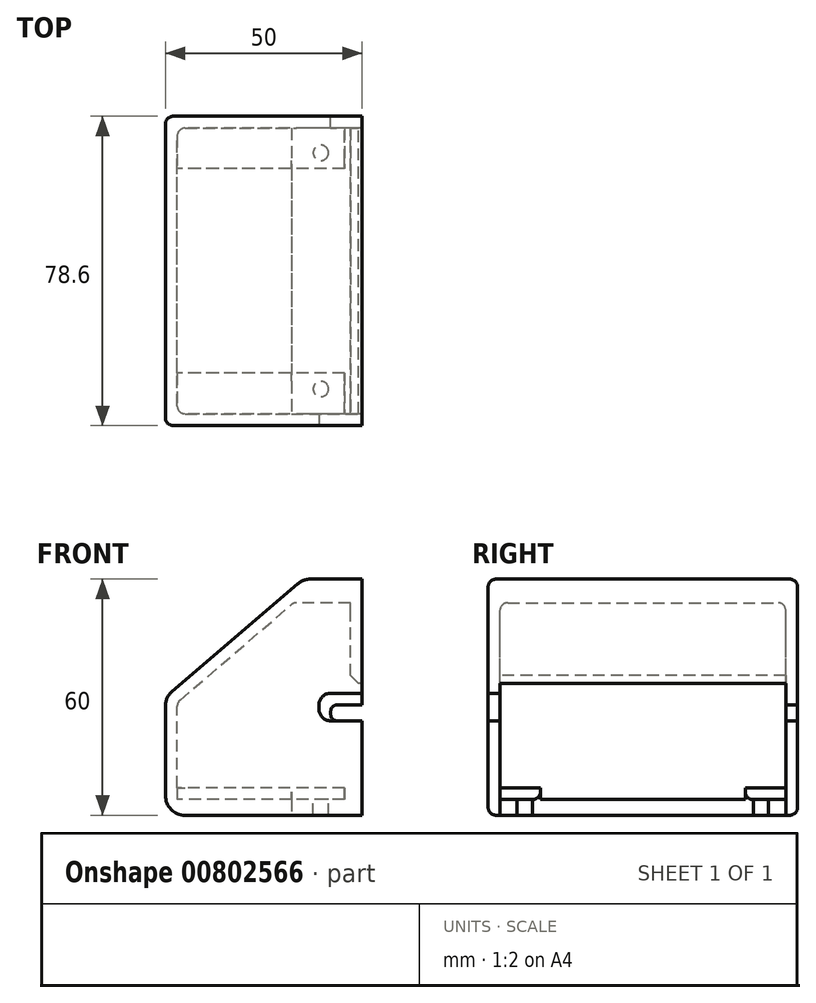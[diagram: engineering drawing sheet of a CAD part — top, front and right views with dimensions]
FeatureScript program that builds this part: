
annotation { "Feature Type Name" : "Feature", "Feature Type Description" : "" }
export const myFeature = defineFeature(function(context is Context, id is Id, definition is map)
    precondition{}
    {
        {
            var Q0;
            Q0=qCreatedBy(makeId("Front.planeOp"),FACE);
            var sketch = newSketch(context, id + "F0", { "sketchPlane" : qUnion([Q0])});
            skLineSegment(sketch, "E0", {"start": v(0, 0) * mm, "end": v(-50, 0) * mm});
            skLineSegment(sketch, "E1", {"start": v(-50, 0) * mm, "end": v(-50, 30) * mm});
            skLineSegment(sketch, "E2", {"start": v(0, 0) * mm, "end": v(0, 60) * mm});
            skLineSegment(sketch, "E3", {"start": v(0, 60) * mm, "end": v(-15, 60) * mm});
            skLineSegment(sketch, "E4", {"start": v(-50, 30) * mm, "end": v(-15, 60) * mm});
            skSolve(sketch);
        }
        {
            var Q0;
            Q0=qSketchRegion(id+"F0",true);
            extrude(context, id + "F1", {"entities" : qUnion([Q0]), "depth" : 78.6 * mm, "offsetDistance" : 25 * mm});
        }
        {
            var Q0;
            Q0=qCreatedBy(makeId("Front.planeOp"),FACE);
            cPlane(context, id + "F2", {"entities" : qUnion([Q0]), "cplaneType" : CPlaneType.OFFSET, "offset" : 3 * mm, "width" : 150 * mm, "height" : 150 * mm});
        }
        {
            var Q0;
            Q0=qCreatedBy(id+"F2.planeOp",FACE);
            var sketch = newSketch(context, id + "F3", { "sketchPlane" : qUnion([Q0])});
            skLineSegment(sketch, "E5", {"start": v(0, 0) * mm, "end": v(0, 4) * mm, "construction": true});
            skLineSegment(sketch, "E6", {"start": v(0, 4) * mm, "end": v(-47, 4) * mm});
            skLineSegment(sketch, "E7", {"start": v(0, 4) * mm, "end": v(0, 33.5) * mm});
            skLineSegment(sketch, "E8", {"start": v(0, 33.5) * mm, "end": v(-3, 33.5) * mm});
            skLineSegment(sketch, "E9", {"start": v(-3, 33.5) * mm, "end": v(-3, 54) * mm});
            skLineSegment(sketch, "E10.0", {"start": v(-47, 28.62) * mm, "end": v(-17.4, 54) * mm});
            skLineSegment(sketch, "E11", {"start": v(-3, 54) * mm, "end": v(-17.4, 54) * mm});
            skLineSegment(sketch, "E12", {"start": v(-47, 4) * mm, "end": v(-47, 28.62) * mm});
            skPoint(sketch, "E13", {"position": v(-47, 28.62) * mm});
            skPoint(sketch, "E14", {"position": v(-17.4, 54) * mm});
            skSolve(sketch);
        }
        {
            var Q0;
            Q0=qSketchRegion(id+"F3",true);
            extrude(context, id + "F4", {"entities" : qUnion([Q0]), "operationType" : NewBodyOperationType.REMOVE, "depth" : 72.6 * mm, "offsetDistance" : 25 * mm});
        }
        {
            var Q0;
            Q0=makeQuery(id+"F1.opExtrude","SWEPT_FACE",FACE,{"disambiguationData":[OSD([sQuery(id+"F0.wireOp",EDGE,"E0")])]});
            var sketch = newSketch(context, id + "F5", { "sketchPlane" : qUnion([Q0])});
            skLineSegment(sketch, "E15", {"start": v(0, 0) * mm, "end": v(0, 3) * mm, "construction": true});
            skLineSegment(sketch, "E16", {"start": v(0, 3) * mm, "end": v(-18, 3) * mm});
            skLineSegment(sketch, "E17", {"start": v(-18, 3) * mm, "end": v(-18, 75.6) * mm});
            skLineSegment(sketch, "E18", {"start": v(-18, 75.6) * mm, "end": v(0, 75.6) * mm});
            skLineSegment(sketch, "E19", {"start": v(0, 75.6) * mm, "end": v(0, 3) * mm});
            skSolve(sketch);
        }
        {
            var Q0;
            Q0=qSketchRegion(id+"F5",true);
            extrude(context, id + "F6", {"entities" : qUnion([Q0]), "operationType" : NewBodyOperationType.REMOVE, "oppositeDirection" : true, "depth" : 5 * mm, "offsetDistance" : 25 * mm});
        }
        {
            var Q0;
            Q0=qCreatedBy(makeId("Front.planeOp"),FACE);
            var sketch = newSketch(context, id + "F7", { "sketchPlane" : qUnion([Q0])});
            skLineSegment(sketch, "E20", {"start": v(0, 0) * mm, "end": v(0, 24) * mm, "construction": true});
            skLineSegment(sketch, "E21", {"start": v(0, 24) * mm, "end": v(0, 28) * mm});
            skLineSegment(sketch, "E22", {"start": v(0, 28) * mm, "end": v(-6.5, 28) * mm});
            skLineSegment(sketch, "E23", {"start": v(-8, 26.5) * mm, "end": v(-8, 25.5) * mm});
            skLineSegment(sketch, "E24", {"start": v(-6.5, 24) * mm, "end": v(0, 24) * mm});
            skPoint(sketch, "E25.visualSharp", {"position": v(-8, 28) * mm});
            skArc(sketch, "E25.filletArc", {"start": v(-6.5, 28) * mm, "mid": v(-7.56, 27.56) * mm, "end": v(-8, 26.5) * mm});
            skPoint(sketch, "E26.visualSharp", {"position": v(-8, 24) * mm});
            skArc(sketch, "E26.filletArc", {"start": v(-8, 25.5) * mm, "mid": v(-7.56, 24.44) * mm, "end": v(-6.5, 24) * mm});
            skSolve(sketch);
        }
        {
            var Q0;
            Q0=qSketchRegion(id+"F7",true);
            extrude(context, id + "F8", {"entities" : qUnion([Q0]), "operationType" : NewBodyOperationType.REMOVE, "depth" : 5 * mm, "offsetDistance" : 25 * mm});
        }
        {
            var Q0;
            Q0=makeQuery(id+"F1.opExtrude","CAP_FACE",FACE,{"disambiguationData":[OSD([sQuery(id+"F0.wireOp",EDGE,"E0"),sQuery(id+"F0.wireOp",EDGE,"E1"),sQuery(id+"F0.wireOp",EDGE,"E2"),sQuery(id+"F0.wireOp",EDGE,"E3"),sQuery(id+"F0.wireOp",EDGE,"E4")])],"isStart":false});
            var sketch = newSketch(context, id + "F9", { "sketchPlane" : qUnion([Q0])});
            skLineSegment(sketch, "E27", {"start": v(0, 0) * mm, "end": v(0, 24) * mm, "construction": true});
            skLineSegment(sketch, "E28", {"start": v(0, 24) * mm, "end": v(0, 31) * mm});
            skLineSegment(sketch, "E29", {"start": v(0, 31) * mm, "end": v(-8, 31) * mm});
            skLineSegment(sketch, "E30", {"start": v(-11, 28) * mm, "end": v(-11, 27) * mm});
            skLineSegment(sketch, "E31", {"start": v(-8, 24) * mm, "end": v(0, 24) * mm});
            skPoint(sketch, "E32.visualSharp", {"position": v(-11, 31) * mm});
            skArc(sketch, "E32.filletArc", {"start": v(-8, 31) * mm, "mid": v(-10.12, 30.12) * mm, "end": v(-11, 28) * mm});
            skPoint(sketch, "E33.visualSharp", {"position": v(-11, 24) * mm});
            skArc(sketch, "E33.filletArc", {"start": v(-11, 27) * mm, "mid": v(-10.12, 24.88) * mm, "end": v(-8, 24) * mm});
            skSolve(sketch);
        }
        {
            var Q0;
            Q0=qSketchRegion(id+"F9",true);
            extrude(context, id + "F10", {"entities" : qUnion([Q0]), "operationType" : NewBodyOperationType.REMOVE, "oppositeDirection" : true, "depth" : 5 * mm, "offsetDistance" : 25 * mm});
        }
        {
            var Q0;
            Q0=makeQuery(id+"FDUO0lFtGd0GRl6_1.opExtrude","CAP_EDGE",EDGE,{"disambiguationData":[OSD([sQuery(id+"Fsfc9BGz6BYfI3k_1.wireOp",EDGE,"UFiVrUBC-8SW0-h0nN-MmJQ-qNYJqojKAnSs")])],"isStart":false});
            var Q1;
            Q1=makeQuery(id+"FDUO0lFtGd0GRl6_1.opExtrude","CAP_EDGE",EDGE,{"disambiguationData":[OSD([sQuery(id+"Fsfc9BGz6BYfI3k_1.wireOp",EDGE,"PaZ7k8qZ-ZSND-94ED-79B7-tNz9TaCtnb4N")])],"isStart":false});
            var Q2;
            Q2=makeQuery(id+"F1.opExtrude","SWEPT_EDGE",EDGE,{"disambiguationData":[OSD([sQuery(id+"F0.wireOp",EDGE,"E3"),sQuery(id+"F0.wireOp",EDGE,"E4")])]});
            var Q3;
            Q3=makeQuery(id+"F1.opExtrude","SWEPT_EDGE",EDGE,{"disambiguationData":[OSD([sQuery(id+"F0.wireOp",EDGE,"E1"),sQuery(id+"F0.wireOp",EDGE,"E4")])]});
            var Q4;
            Q4=makeQuery(id+"F1.opExtrude","SWEPT_EDGE",EDGE,{"disambiguationData":[OSD([sQuery(id+"F0.wireOp",EDGE,"E0"),sQuery(id+"F0.wireOp",EDGE,"E1")])]});
            fillet(context, id + "F11", {"entities" : qUnion([Q0, Q1, Q2, Q3, Q4]), "radius" : 5 * mm, "tangentPropagation" : true, "allowEdgeOverflow" : false});
        }
        {
            var Q0;
            Q0=makeQuery(id+"FDUO0lFtGd0GRl6_1.opExtrude","SWEPT_EDGE",EDGE,{"disambiguationData":[OSD([sQuery(id+"Fsfc9BGz6BYfI3k_1.wireOp",EDGE,"2MNWM4fN-UouW-SbYd-ouZd-wXEaQsLsKWml"),sQuery(id+"Fsfc9BGz6BYfI3k_1.wireOp",EDGE,"UFiVrUBC-8SW0-h0nN-MmJQ-qNYJqojKAnSs")])]});
            var Q1;
            Q1=makeQuery(id+"F1.opExtrude","CAP_EDGE",EDGE,{"disambiguationData":[OSD([sQuery(id+"F0.wireOp",EDGE,"E4")])],"isStart":true});
            var Q2;
            Q2=makeQuery(id+"F1.opExtrude","CAP_EDGE",EDGE,{"disambiguationData":[OSD([sQuery(id+"F0.wireOp",EDGE,"E4")])],"isStart":false});
            fillet(context, id + "F12", {"entities" : qUnion([Q0, Q1, Q2]), "radius" : 2 * mm, "tangentPropagation" : true, "allowEdgeOverflow" : false});
        }
        {
            var Q0;
            Q0=makeQuery(id+"F4.boolean.opBoolean","COPY",FACE,{"derivedFrom":makeQuery(id+"F4.opExtrude","SWEPT_FACE",FACE,{"disambiguationData":[OSD([sQuery(id+"F3.wireOp",EDGE,"E12")])]})});
            var sketch = newSketch(context, id + "F13", { "sketchPlane" : qUnion([Q0])});
            skLineSegment(sketch, "E34", {"start": v(0, 0) * mm, "end": v(-3, 0) * mm, "construction": true});
            skLineSegment(sketch, "E35", {"start": v(-75.6, 0) * mm, "end": v(-78.6, 0) * mm, "construction": true});
            skLineSegment(sketch, "E36", {"start": v(-3, 0) * mm, "end": v(-39.3, 0) * mm, "construction": true});
            skLineSegment(sketch, "E37", {"start": v(-39.3, 0) * mm, "end": v(-39.3, 4) * mm, "construction": true});
            skLineSegment(sketch, "E38", {"start": v(-39.3, 4) * mm, "end": v(-39.3, 7) * mm, "construction": true});
            skLineSegment(sketch, "E39", {"start": v(-39.3, 7) * mm, "end": v(-3, 7) * mm, "construction": true});
            skLineSegment(sketch, "E40", {"start": v(-3, 7) * mm, "end": v(-13.3, 7) * mm});
            skLineSegment(sketch, "E41", {"start": v(-13.3, 7) * mm, "end": v(-13.3, 4) * mm});
            skLineSegment(sketch, "E42", {"start": v(-13.3, 4) * mm, "end": v(-3, 4) * mm});
            skLineSegment(sketch, "E43", {"start": v(-3, 4) * mm, "end": v(-3, 7) * mm});
            skLineSegment(sketch, "E44.MirrorCS", {"start": v(-75.6, 4) * mm, "end": v(-75.6, 7) * mm});
            skLineSegment(sketch, "E45.MirrorCS", {"start": v(-65.3, 7) * mm, "end": v(-65.3, 4) * mm});
            skLineSegment(sketch, "E46.MirrorCS", {"start": v(-65.3, 4) * mm, "end": v(-75.6, 4) * mm});
            skLineSegment(sketch, "E47", {"start": v(-65.3, 7) * mm, "end": v(-75.6, 7) * mm});
            skSolve(sketch);
        }
        {
            var Q0;
            Q0=qSketchRegion(id+"F13",true);
            extrude(context, id + "F14", {"entities" : qUnion([Q0]), "operationType" : NewBodyOperationType.ADD, "depth" : 42.5 * mm, "offsetDistance" : 25 * mm});
        }
        {
            var Q0;
            Q0=qCreatedBy(makeId("Top.planeOp"),FACE);
            cPlane(context, id + "F15", {"entities" : qUnion([Q0]), "cplaneType" : CPlaneType.OFFSET, "offset" : 4 * mm, "width" : 150 * mm, "height" : 150 * mm});
        }
        {
            var Q0;
            Q0=qCreatedBy(id+"F15.planeOp",FACE);
            var sketch = newSketch(context, id + "F16", { "sketchPlane" : qUnion([Q0])});
            skLineSegment(sketch, "E48", {"start": v(0, 0) * mm, "end": v(0, -3) * mm, "construction": true});
            skLineSegment(sketch, "E49", {"start": v(0, -3) * mm, "end": v(-4, -3) * mm, "construction": true});
            skLineSegment(sketch, "E50", {"start": v(-4, -3) * mm, "end": v(-10.5, -3) * mm, "construction": true});
            skLineSegment(sketch, "E51", {"start": v(-10.5, -3) * mm, "end": v(-10.5, -3.3) * mm, "construction": true});
            skLineSegment(sketch, "E52", {"start": v(-10.5, -3.3) * mm, "end": v(-10.5, -9.3) * mm, "construction": true});
            skLineSegment(sketch, "E53", {"start": v(-10.5, -9.3) * mm, "end": v(-10.5, -69.3) * mm, "construction": true});
            skLineSegment(sketch, "E54", {"start": v(-10.5, -69.3) * mm, "end": v(-10.5, -75.3) * mm, "construction": true});
            skLineSegment(sketch, "E55", {"start": v(-10.5, -75.3) * mm, "end": v(-10.5, -75.6) * mm, "construction": true});
            skLineSegment(sketch, "E56", {"start": v(-10.5, -75.6) * mm, "end": v(-10.5, -78.6) * mm, "construction": true});
            skCircle(sketch, "E57", {"center": v(-10.5, -9.3) * mm, "radius": 1.95 * mm});
            skCircle(sketch, "E58", {"center": v(-10.5, -69.3) * mm, "radius": 1.95 * mm});
            skLineSegment(sketch, "E59", {"start": v(-10.5, -3) * mm, "end": v(-14, -3) * mm, "construction": true});
            skLineSegment(sketch, "E60", {"start": v(-14, -3) * mm, "end": v(-18, -3) * mm, "construction": true});
            skSolve(sketch);
        }
        {
            var Q0;
            Q0=qSketchRegion(id+"F16",true);
            extrude(context, id + "F17", {"entities" : qUnion([Q0]), "operationType" : NewBodyOperationType.ADD, "oppositeDirection" : true, "depth" : 4 * mm, "offsetDistance" : 25 * mm});
        }
        {
            var Q0;
            Q0=makeQuery(id+"F4.boolean.opBoolean","COPY",EDGE,{"derivedFrom":makeQuery(id+"F4.opExtrude","SWEPT_EDGE",EDGE,{"disambiguationData":[OSD([sQuery(id+"F3.wireOp",EDGE,"E8"),sQuery(id+"F3.wireOp",EDGE,"E9")])]})});
            chamfer(context, id + "F18", {"entities" : qUnion([Q0]), "width" : 2 * mm, "tangentPropagation" : true});
        }
        {
            var Q0;
            Q0=makeQuery(id+"F14.opExtrude","CAP_EDGE",EDGE,{"disambiguationData":[OSD([sQuery(id+"F13.wireOp",EDGE,"E40")])],"isStart":true});
            var Q1;
            Q1=makeQuery(id+"F14.opExtrude","CAP_EDGE",EDGE,{"disambiguationData":[OSD([sQuery(id+"F13.wireOp",EDGE,"E41")])],"isStart":true});
            var Q2;
            {var subQ0=sQuery(id+"F3.wireOp",EDGE,"E6");var subQ1=sQuery(id+"F13.wireOp",EDGE,"E41");Q2=makeQuery(id+"F14.boolean.opBoolean","SPLIT",EDGE,{"disambiguationData":[topologyDisambiguationEdgeConnected([makeQuery(id+"F4.boolean.opBoolean","COPY",FACE,{"derivedFrom":makeQuery(id+"F4.opExtrude","SWEPT_FACE",FACE,{"disambiguationData":[OSD([subQ0])]})})])],"derivedFrom":makeQuery(id+"F14.opExtrude","SWEPT_EDGE",EDGE,{"disambiguationData":[OSD([subQ0,sQuery(id+"F3.wireOp",EDGE,"E12"),subQ1,sQuery(id+"F13.wireOp",EDGE,"E42")])]})});}
            var Q3;
            Q3=makeQuery(id+"F14.opExtrude","CAP_EDGE",EDGE,{"disambiguationData":[OSD([sQuery(id+"F13.wireOp",EDGE,"E47")])],"isStart":true});
            var Q4;
            Q4=makeQuery(id+"F14.opExtrude","CAP_EDGE",EDGE,{"disambiguationData":[OSD([sQuery(id+"F13.wireOp",EDGE,"E45.MirrorCS")])],"isStart":true});
            var Q5;
            {var subQ0=sQuery(id+"F3.wireOp",EDGE,"E6");var subQ1=sQuery(id+"F13.wireOp",EDGE,"E45.MirrorCS");Q5=makeQuery(id+"F14.boolean.opBoolean","SPLIT",EDGE,{"disambiguationData":[topologyDisambiguationEdgeConnected([makeQuery(id+"F4.boolean.opBoolean","COPY",FACE,{"derivedFrom":makeQuery(id+"F4.opExtrude","SWEPT_FACE",FACE,{"disambiguationData":[OSD([subQ0])]})})])],"derivedFrom":makeQuery(id+"F14.opExtrude","SWEPT_EDGE",EDGE,{"disambiguationData":[OSD([subQ0,sQuery(id+"F3.wireOp",EDGE,"E12"),subQ1,sQuery(id+"F13.wireOp",EDGE,"E46.MirrorCS")])]})});}
            var Q6;
            Q6=makeQuery(id+"F14.opExtrude","SWEPT_EDGE",EDGE,{"disambiguationData":[OSD([sQuery(id+"F3.wireOp",EDGE,"E12"),sQuery(id+"F13.wireOp",EDGE,"E44.MirrorCS"),sQuery(id+"F13.wireOp",EDGE,"E47")])]});
            var Q7;
            Q7=makeQuery(id+"F14.opExtrude","SWEPT_EDGE",EDGE,{"disambiguationData":[OSD([sQuery(id+"F3.wireOp",EDGE,"E12"),sQuery(id+"F13.wireOp",EDGE,"E40"),sQuery(id+"F13.wireOp",EDGE,"E43")])]});
            var Q8;
            Q8=makeQuery(id+"F4.boolean.opBoolean","COPY",EDGE,{"derivedFrom":makeQuery(id+"F4.opExtrude","CAP_EDGE",EDGE,{"disambiguationData":[OSD([sQuery(id+"F3.wireOp",EDGE,"E12")])],"isStart":true})});
            var Q9;
            Q9=makeQuery(id+"F4.boolean.opBoolean","COPY",EDGE,{"derivedFrom":makeQuery(id+"F4.opExtrude","CAP_EDGE",EDGE,{"disambiguationData":[OSD([sQuery(id+"F3.wireOp",EDGE,"E10.0")])],"isStart":true})});
            var Q10;
            Q10=makeQuery(id+"F4.boolean.opBoolean","COPY",EDGE,{"derivedFrom":makeQuery(id+"F4.opExtrude","SWEPT_EDGE",EDGE,{"disambiguationData":[OSD([sQuery(id+"F3.wireOp",EDGE,"E10.0"),sQuery(id+"F3.wireOp",EDGE,"E12")])]})});
            var Q11;
            Q11=makeQuery(id+"F4.boolean.opBoolean","COPY",EDGE,{"derivedFrom":makeQuery(id+"F4.opExtrude","CAP_EDGE",EDGE,{"disambiguationData":[OSD([sQuery(id+"F3.wireOp",EDGE,"E12")])],"isStart":false})});
            var Q12;
            Q12=makeQuery(id+"F4.boolean.opBoolean","COPY",EDGE,{"derivedFrom":makeQuery(id+"F4.opExtrude","CAP_EDGE",EDGE,{"disambiguationData":[OSD([sQuery(id+"F3.wireOp",EDGE,"E10.0")])],"isStart":false})});
            var Q13;
            Q13=makeQuery(id+"F4.boolean.opBoolean","COPY",EDGE,{"derivedFrom":makeQuery(id+"F4.opExtrude","SWEPT_EDGE",EDGE,{"disambiguationData":[OSD([sQuery(id+"F3.wireOp",EDGE,"E10.0"),sQuery(id+"F3.wireOp",EDGE,"E11")])]})});
            var Q14;
            Q14=makeQuery(id+"F4.boolean.opBoolean","COPY",EDGE,{"derivedFrom":makeQuery(id+"F4.opExtrude","CAP_EDGE",EDGE,{"disambiguationData":[OSD([sQuery(id+"F3.wireOp",EDGE,"E11")])],"isStart":true})});
            var Q15;
            Q15=makeQuery(id+"F4.boolean.opBoolean","COPY",EDGE,{"derivedFrom":makeQuery(id+"F4.opExtrude","CAP_EDGE",EDGE,{"disambiguationData":[OSD([sQuery(id+"F3.wireOp",EDGE,"E11")])],"isStart":false})});
            fillet(context, id + "F19", {"entities" : qUnion([Q0, Q1, Q2, Q3, Q4, Q5, Q6, Q7, Q8, Q9, Q10, Q11, Q12, Q13, Q14, Q15]), "radius" : 2 * mm, "tangentPropagation" : true, "allowEdgeOverflow" : false});
        }
    });
